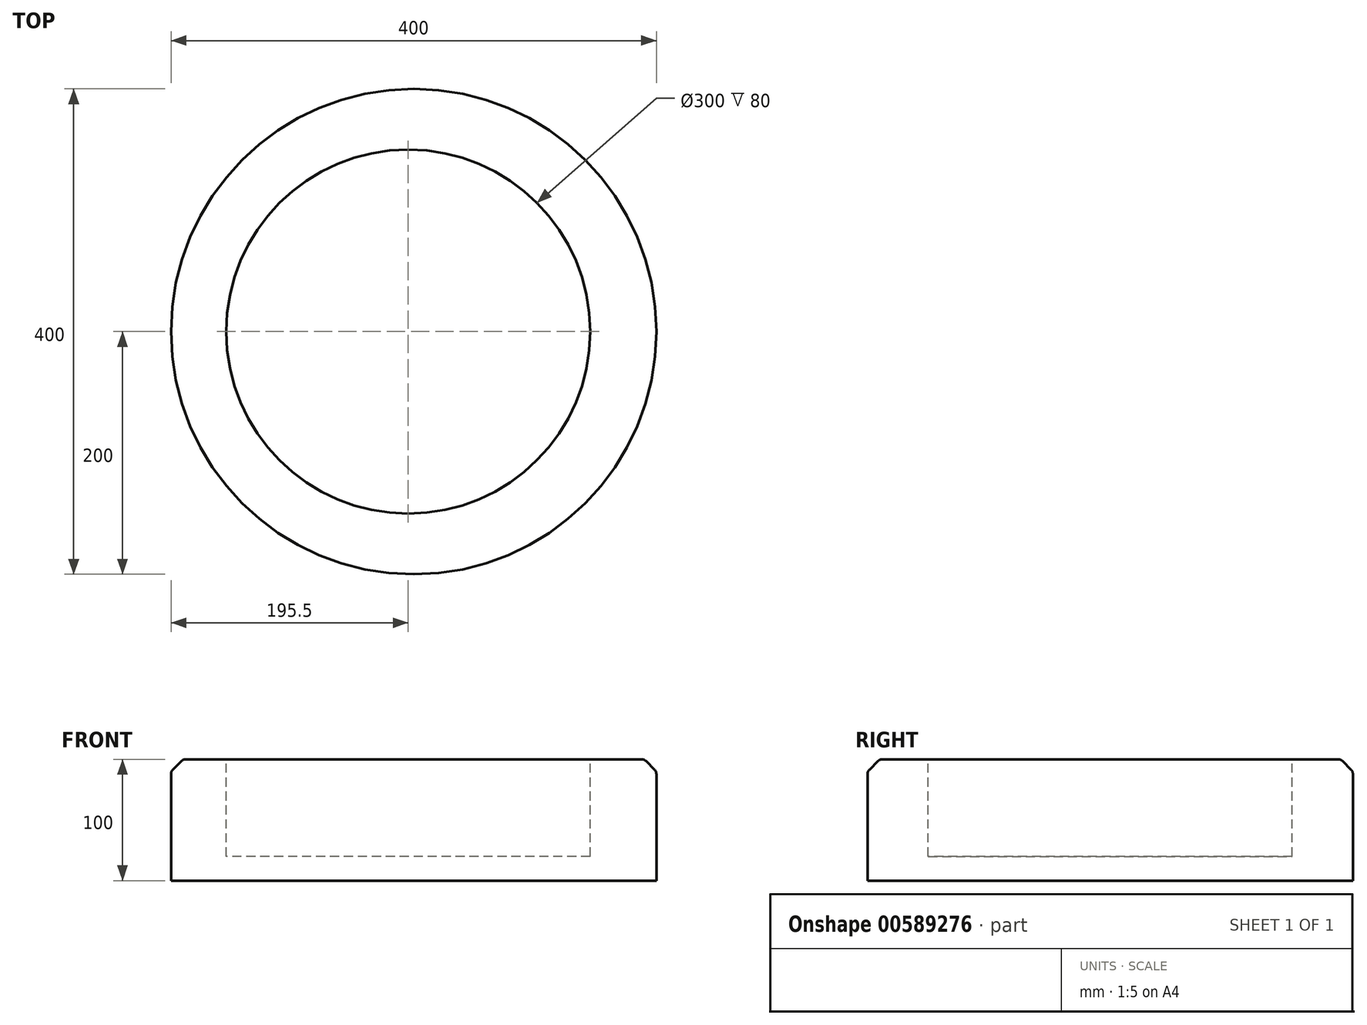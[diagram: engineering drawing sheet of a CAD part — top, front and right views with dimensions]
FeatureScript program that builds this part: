
annotation { "Feature Type Name" : "Feature", "Feature Type Description" : "" }
export const myFeature = defineFeature(function(context is Context, id is Id, definition is map)
    precondition{}
    {
        {
            var Q0;
            Q0=qCreatedBy(makeId("Top.planeOp"),FACE);
            var sketch = newSketch(context, id + "F0", { "sketchPlane" : qUnion([Q0])});
            skCircle(sketch, "E0", {"center": v(4.5, 0) * mm, "radius": 200 * mm});
            skSolve(sketch);
        }
        {
            var Q0;
            Q0=makeQuery(id+"F0.imprint","IMPRINT",FACE,{"disambiguationData":[TD([[makeQuery(id+"F0.imprint","IMPRINT",EDGE,{"derivedFrom":sQuery(id+"F0.wireOp",EDGE,"E0")}),1.0]])]});
            extrude(context, id + "F1", {"entities" : qUnion([Q0]), "depth" : 100 * mm, "offsetDistance" : 25 * mm});
        }
        {
            var Q0;
            Q0=makeQuery(id+"F1.opExtrude","CAP_FACE",FACE,{"disambiguationData":[OSD([sQuery(id+"F0.wireOp",EDGE,"E0")])],"isStart":false});
            var sketch = newSketch(context, id + "F2", { "sketchPlane" : qUnion([Q0])});
            skCircle(sketch, "E1", {"center": v(0, 0) * mm, "radius": 150 * mm});
            skSolve(sketch);
        }
        {
            var Q0;
            Q0=makeQuery(id+"F2.imprint","IMPRINT",FACE,{"disambiguationData":[TD([[makeQuery(id+"F2.imprint","IMPRINT",EDGE,{"derivedFrom":sQuery(id+"F2.wireOp",EDGE,"E1")}),1.0]])]});
            extrude(context, id + "F3", {"entities" : qUnion([Q0]), "operationType" : NewBodyOperationType.REMOVE, "oppositeDirection" : true, "depth" : 80 * mm, "offsetDistance" : 25 * mm});
        }
        {
            var Q0;
            Q0=makeQuery(id+"F1.opExtrude","CAP_EDGE",EDGE,{"disambiguationData":[OSD([sQuery(id+"F0.wireOp",EDGE,"E0")])],"isStart":false});
            chamfer(context, id + "F4", {"entities" : qUnion([Q0]), "width" : 10 * mm, "tangentPropagation" : true});
        }
        {
            var Q0;
            {var subQ0=sQuery(id+"F0.wireOp",EDGE,"E0");Q0=makeQuery(id+"F4.opChamfer","BLEND_EDGE",EDGE,{"blendedFrom":[makeQuery(id+"F1.opExtrude","CAP_EDGE",EDGE,{"disambiguationData":[OSD([subQ0])],"isStart":false}),makeQuery(id+"F1.opExtrude","CAP_FACE",FACE,{"disambiguationData":[OSD([subQ0])],"isStart":false})],"blendedInto":[makeQuery(id+"F1.opExtrude","CAP_FACE",FACE,{"disambiguationData":[OSD([subQ0])],"isStart":false})]});}
            fillet(context, id + "F5", {"entities" : qUnion([Q0]), "radius" : 5 * mm, "tangentPropagation" : true, "allowEdgeOverflow" : false});
        }
        {
            var Q0;
            {var subQ0=sQuery(id+"F0.wireOp",EDGE,"E0");Q0=makeQuery(id+"F4.opChamfer","BLEND_EDGE",EDGE,{"blendedFrom":[makeQuery(id+"F1.opExtrude","CAP_EDGE",EDGE,{"disambiguationData":[OSD([subQ0])],"isStart":false}),makeQuery(id+"F1.opExtrude","SWEPT_FACE",FACE,{"disambiguationData":[OSD([subQ0])]})],"blendedInto":[makeQuery(id+"F1.opExtrude","SWEPT_FACE",FACE,{"disambiguationData":[OSD([subQ0])]})]});}
            fillet(context, id + "F6", {"entities" : qUnion([Q0]), "radius" : 5 * mm, "tangentPropagation" : true, "allowEdgeOverflow" : false});
        }
    });
